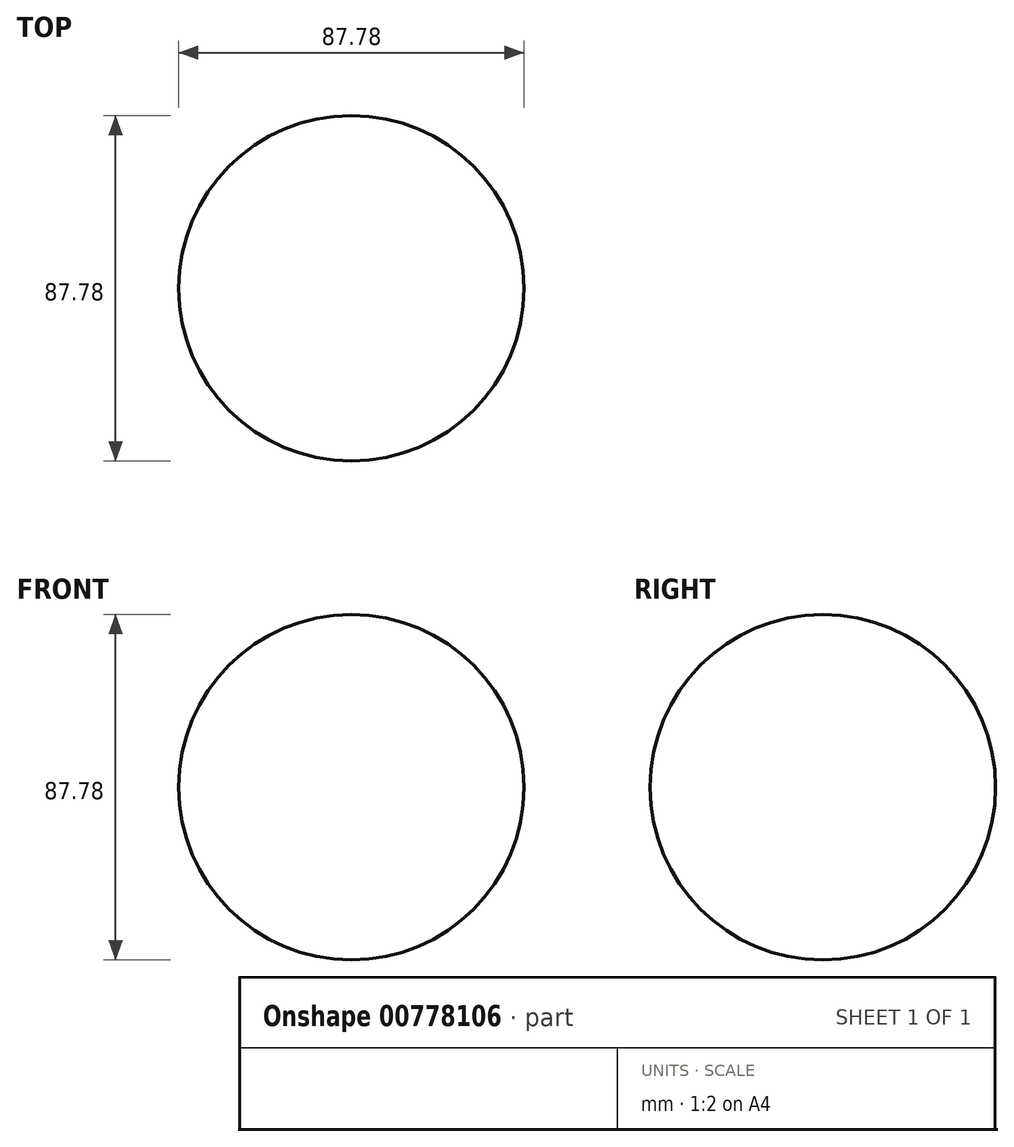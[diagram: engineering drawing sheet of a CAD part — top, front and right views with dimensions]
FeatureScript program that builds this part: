
annotation { "Feature Type Name" : "Feature", "Feature Type Description" : "" }
export const myFeature = defineFeature(function(context is Context, id is Id, definition is map)
    precondition{}
    {
        {
            var Q0;
            Q0=qCreatedBy(makeId("Front.planeOp"),FACE);
            var sketch = newSketch(context, id + "F0", { "sketchPlane" : qUnion([Q0])});
            skArc(sketch, "E0", {"start": v(0, 43.89) * mm, "mid": v(-43.89, 0) * mm, "end": v(0, -43.89) * mm});
            skLineSegment(sketch, "E1", {"start": v(0, 0) * mm, "end": v(0, 83.4) * mm, "construction": true});
            skLineSegment(sketch, "E2", {"start": v(0, 0) * mm, "end": v(0, -53.52) * mm, "construction": true});
            skLineSegment(sketch, "E3", {"start": v(0, 43.89) * mm, "end": v(0, -43.89) * mm});
            skSolve(sketch);
        }
        {
            var Q0;
            Q0=makeQuery(id+"F0.imprint","IMPRINT",FACE,{"disambiguationData":[TD([[makeQuery(id+"F0.imprint","IMPRINT",EDGE,{"derivedFrom":sQuery(id+"F0.wireOp",EDGE,"E0")}),1.0]])]});
            var Q1;
            Q1=sQuery(id+"F0.wireOp",EDGE,"E1");
            revolve(context, id + "F1", {"surfaceOperationType" : NewSurfaceOperationType.NEW, "entities" : qUnion([Q0]), "axis" : qUnion([Q1]), "revolveType" : RevolveType.FULL});
        }
    });
